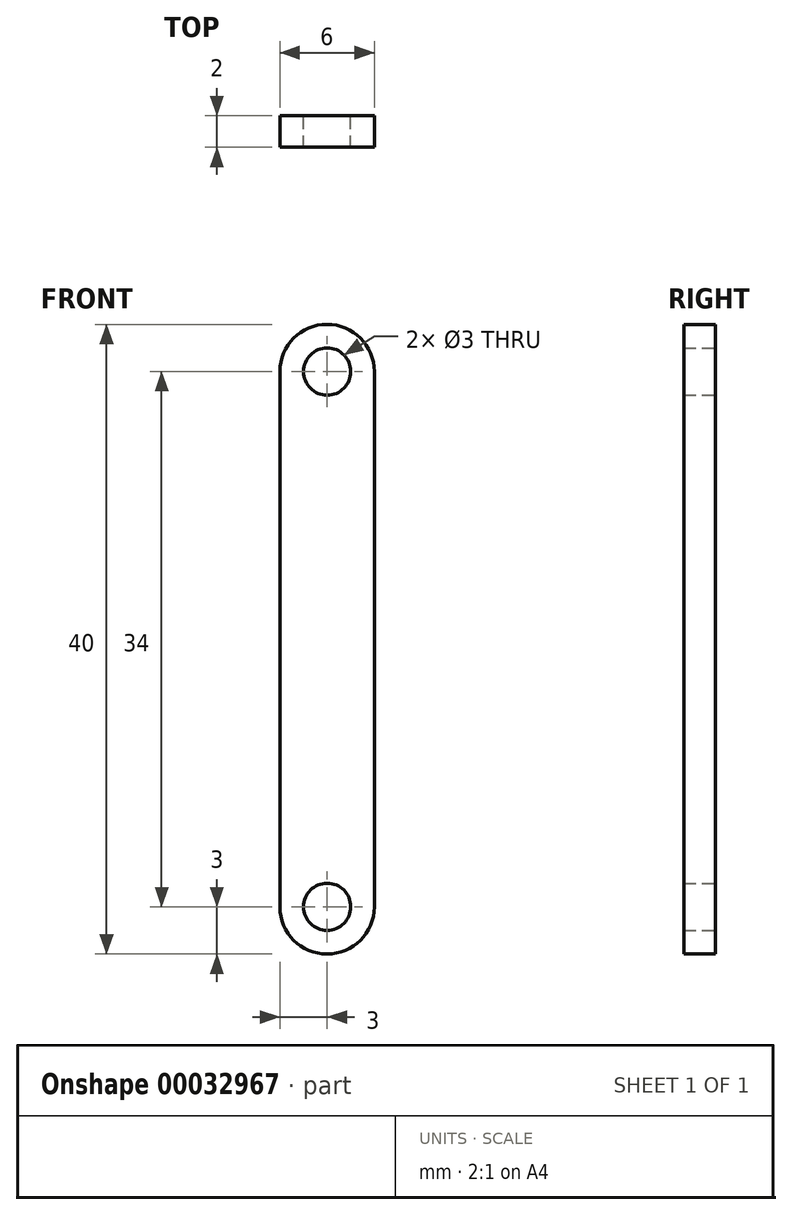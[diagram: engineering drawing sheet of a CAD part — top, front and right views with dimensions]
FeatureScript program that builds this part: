
annotation { "Feature Type Name" : "Feature", "Feature Type Description" : "" }
export const myFeature = defineFeature(function(context is Context, id is Id, definition is map)
    precondition{}
    {
        {
            var Q0;
            Q0=qCreatedBy(makeId("Front.planeOp"),FACE);
            var sketch = newSketch(context, id + "F0", { "sketchPlane" : qUnion([Q0])});
            skLineSegment(sketch, "E0.rect.left", {"start": v(3, -9) * mm, "end": v(3, 25) * mm});
            skLineSegment(sketch, "E0.rect.right", {"start": v(-3, -9) * mm, "end": v(-3, 25) * mm});
            skPoint(sketch, "E0.rect.middle", {"position": v(0, 0) * mm});
            skArc(sketch, "E1", {"start": v(3, 25) * mm, "mid": v(0, 28) * mm, "end": v(-3, 25) * mm});
            skCircle(sketch, "E2", {"center": v(0, 25) * mm, "radius": 1.5 * mm});
            skCircle(sketch, "E3", {"center": v(0, -9) * mm, "radius": 1.5 * mm});
            skArc(sketch, "E4", {"start": v(-3, -9) * mm, "mid": v(0, -12) * mm, "end": v(3, -9) * mm});
            skSolve(sketch);
        }
        {
            var Q0;
            Q0=qSketchRegion(id+"F0",true);
            extrude(context, id + "F1", {"entities" : qUnion([Q0]), "depth" : 2 * mm});
        }
    });
